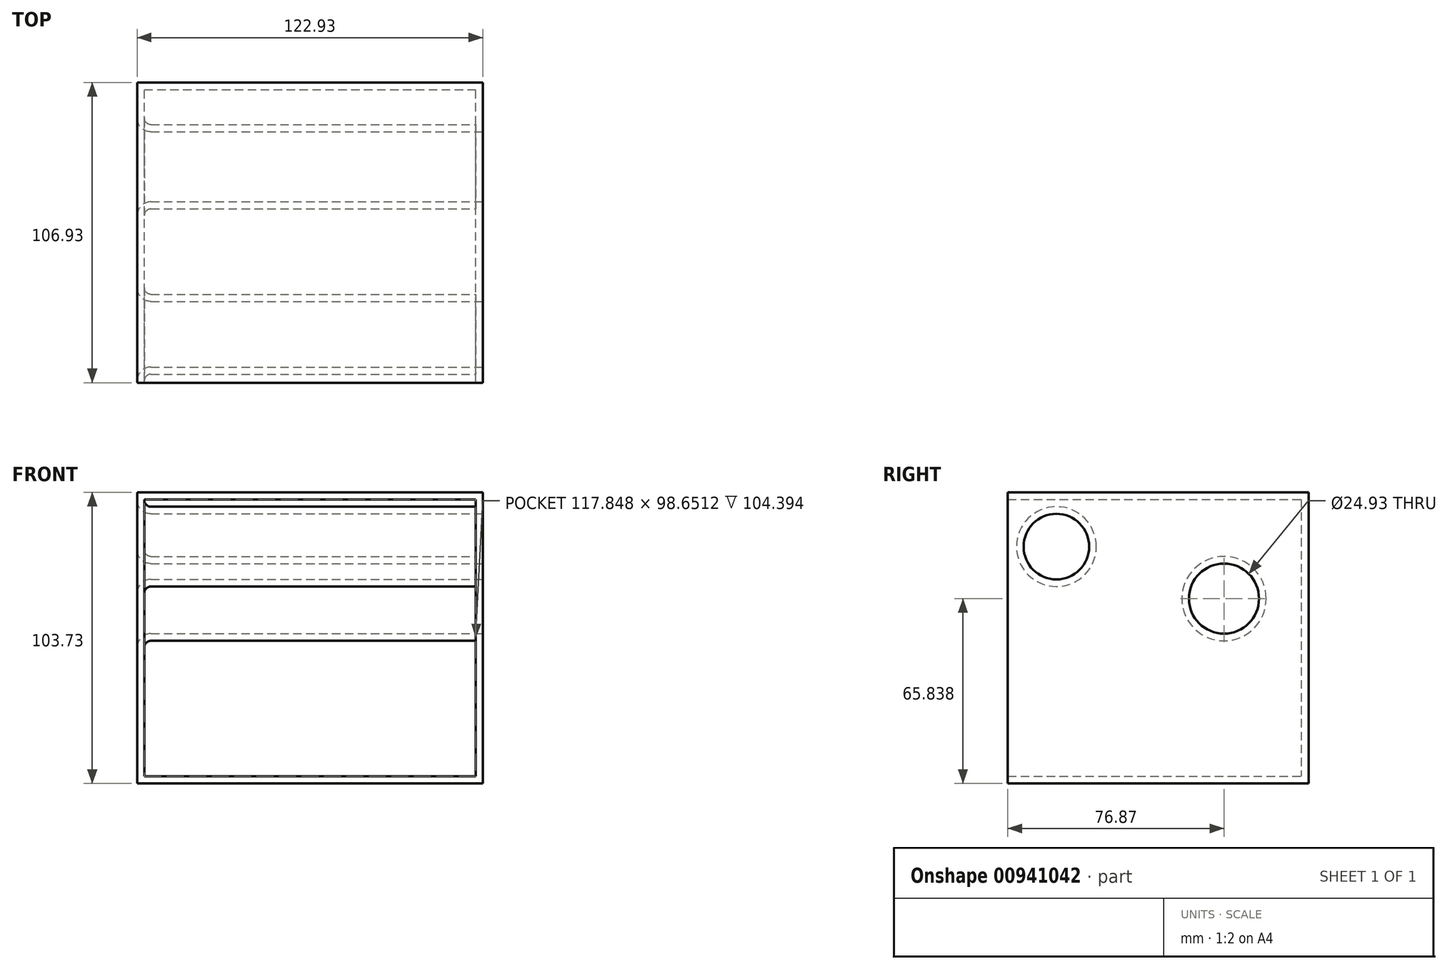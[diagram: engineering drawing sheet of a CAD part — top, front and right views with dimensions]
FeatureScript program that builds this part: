
annotation { "Feature Type Name" : "Feature", "Feature Type Description" : "" }
export const myFeature = defineFeature(function(context is Context, id is Id, definition is map)
    precondition{}
    {
        {
            var Q0;
            Q0=qCreatedBy(makeId("Front.planeOp"),FACE);
            var sketch = newSketch(context, id + "F0", { "sketchPlane" : qUnion([Q0])});
            skLineSegment(sketch, "E0.bottom", {"start": v(-60.96, 51.7) * mm, "end": v(61.97, 51.7) * mm});
            skLineSegment(sketch, "E0.top", {"start": v(-60.96, -52.03) * mm, "end": v(61.97, -52.03) * mm});
            skLineSegment(sketch, "E0.left", {"start": v(-60.96, 51.7) * mm, "end": v(-60.96, -52.03) * mm});
            skLineSegment(sketch, "E0.right", {"start": v(61.97, 51.7) * mm, "end": v(61.97, -52.03) * mm});
            skSolve(sketch);
        }
        {
            var Q0;
            Q0=makeQuery(id+"F0.imprint","IMPRINT",FACE,{"disambiguationData":[TD([[makeQuery(id+"F0.imprint","IMPRINT",EDGE,{"derivedFrom":sQuery(id+"F0.wireOp",EDGE,"E0.bottom")}),-1.0]])]});
            extrude(context, id + "F1", {"entities" : qUnion([Q0]), "depth" : 106.93 * mm, "offsetDistance" : 25.4 * mm});
        }
        {
            var Q0;
            Q0=makeQuery(id+"F1.opExtrude","SWEPT_FACE",FACE,{"disambiguationData":[OSD([sQuery(id+"F0.wireOp",EDGE,"E0.right")])]});
            var sketch = newSketch(context, id + "F2", { "sketchPlane" : qUnion([Q0])});
            skCircle(sketch, "E1", {"center": v(-89.67, 32.33) * mm, "radius": 11.67 * mm});
            skCircle(sketch, "E2", {"center": v(-30.06, 13.8) * mm, "radius": 12.47 * mm});
            skSolve(sketch);
        }
        {
            var Q0;
            Q0=makeQuery(id+"F2.imprint","IMPRINT",FACE,{"disambiguationData":[TD([[makeQuery(id+"F2.imprint","IMPRINT",EDGE,{"derivedFrom":sQuery(id+"F2.wireOp",EDGE,"E1")}),1.0]])]});
            var Q1;
            Q1=makeQuery(id+"F2.imprint","IMPRINT",FACE,{"disambiguationData":[TD([[makeQuery(id+"F2.imprint","IMPRINT",EDGE,{"derivedFrom":sQuery(id+"F2.wireOp",EDGE,"E2")}),1.0]])]});
            extrude(context, id + "F3", {"entities" : qUnion([Q0, Q1]), "operationType" : NewBodyOperationType.REMOVE, "endBound" : BoundingType.THROUGH_ALL, "oppositeDirection" : true, "depth" : 49.02 * mm, "offsetDistance" : 25.4 * mm});
        }
        {
            var Q0;
            Q0=makeQuery(id+"F3.boolean.opBoolean","COPY",EDGE,{"derivedFrom":makeQuery(id+"F3.opExtrude","CAP_EDGE",EDGE,{"disambiguationData":[OSD([sQuery(id+"F2.wireOp",EDGE,"E1")])],"isStart":true})});
            var Q1;
            Q1=makeQuery(id+"F3.boolean.opBoolean","COPY",EDGE,{"derivedFrom":makeQuery(id+"F3.opExtrude","CAP_EDGE",EDGE,{"disambiguationData":[OSD([sQuery(id+"F2.wireOp",EDGE,"E2")])],"isStart":true})});
            var Q2;
            Q2=makeQuery(id+"F3.boolean.opBoolean","INTERSECT",EDGE,{"derivedFrom":[makeQuery(id+"F1.opExtrude","SWEPT_FACE",FACE,{"disambiguationData":[OSD([sQuery(id+"F0.wireOp",EDGE,"E0.left")])]}),makeQuery(id+"F3.opExtrude","SWEPT_FACE",FACE,{"disambiguationData":[OSD([sQuery(id+"F2.wireOp",EDGE,"E1")])]})]});
            var Q3;
            Q3=makeQuery(id+"F3.boolean.opBoolean","INTERSECT",EDGE,{"derivedFrom":[makeQuery(id+"F1.opExtrude","SWEPT_FACE",FACE,{"disambiguationData":[OSD([sQuery(id+"F0.wireOp",EDGE,"E0.left")])]}),makeQuery(id+"F3.opExtrude","SWEPT_FACE",FACE,{"disambiguationData":[OSD([sQuery(id+"F2.wireOp",EDGE,"E2")])]})]});
            fillet(context, id + "F4", {"entities" : qUnion([Q0, Q1, Q2, Q3]), "radius" : 4.9 * mm, "tangentPropagation" : true, "allowEdgeOverflow" : false});
        }
        {
            var Q0;
            Q0=makeQuery(id+"F1.opExtrude","CAP_FACE",FACE,{"disambiguationData":[OSD([sQuery(id+"F0.wireOp",EDGE,"E0.bottom"),sQuery(id+"F0.wireOp",EDGE,"E0.top"),sQuery(id+"F0.wireOp",EDGE,"E0.left"),sQuery(id+"F0.wireOp",EDGE,"E0.right")])],"isStart":false});
            shell(context, id + "F5", {"entities" : qUnion([Q0]), "thickness" : 2.54 * mm});
        }
    });
